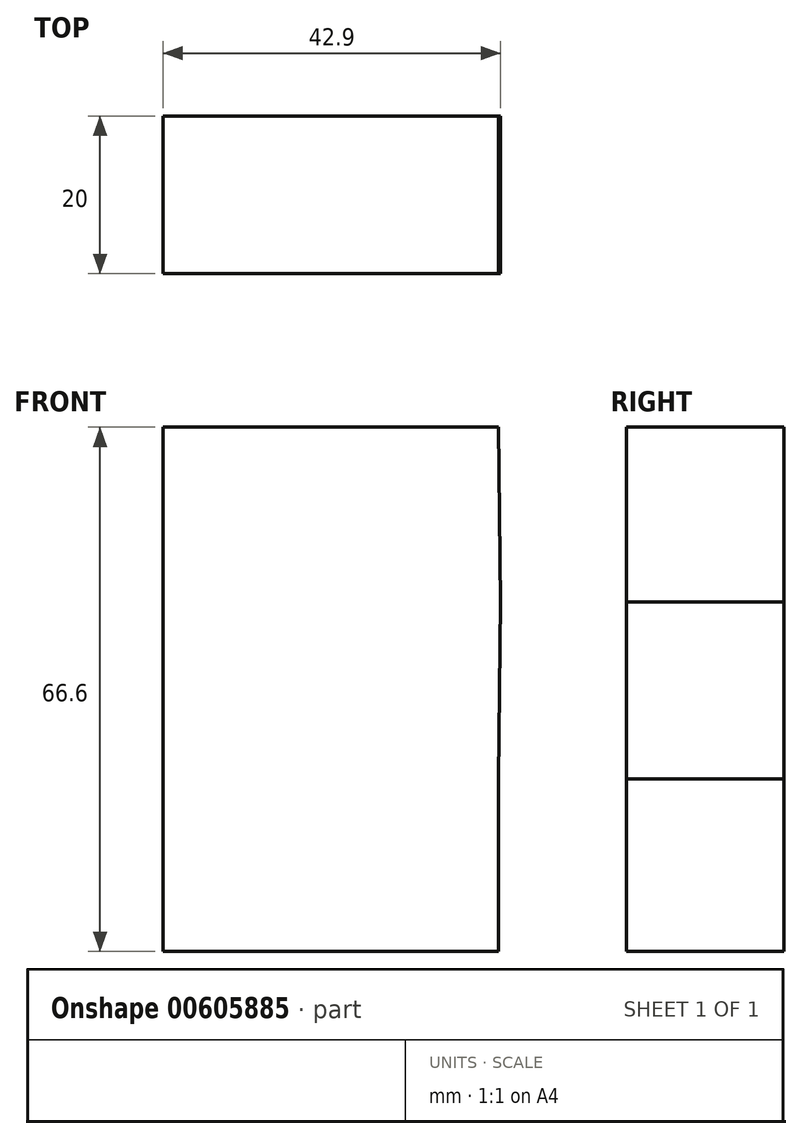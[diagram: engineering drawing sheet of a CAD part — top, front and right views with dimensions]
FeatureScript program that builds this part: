
annotation { "Feature Type Name" : "Feature", "Feature Type Description" : "" }
export const myFeature = defineFeature(function(context is Context, id is Id, definition is map)
    precondition{}
    {
        {
            var Q0;
            Q0=qCreatedBy(makeId("Front.planeOp"),FACE);
            var sketch = newSketch(context, id + "F0", { "sketchPlane" : qUnion([Q0])});
            skLineSegment(sketch, "E0", {"start": v(-5.55, 30.3) * mm, "end": v(-25.35, 30.3) * mm});
            skLineSegment(sketch, "E1", {"start": v(-25.35, 30.3) * mm, "end": v(-25.35, 8.1) * mm});
            skLineSegment(sketch, "E2", {"start": v(-25.35, 8.1) * mm, "end": v(-5.25, 8.1) * mm});
            skLineSegment(sketch, "E3", {"start": v(-5.55, 30.3) * mm, "end": v(-5.25, 8.1) * mm});
            skLineSegment(sketch, "E4", {"start": v(-25.35, 8.1) * mm, "end": v(-25.35, -14.4) * mm});
            skLineSegment(sketch, "E5", {"start": v(-25.35, -14.4) * mm, "end": v(-5.55, -14.4) * mm});
            skLineSegment(sketch, "E6", {"start": v(-5.55, -14.4) * mm, "end": v(-5.25, 8.1) * mm});
            skLineSegment(sketch, "E7", {"start": v(-25.35, -14.4) * mm, "end": v(-25.35, -36.3) * mm});
            skLineSegment(sketch, "E8", {"start": v(-25.35, -36.3) * mm, "end": v(-5.55, -36.3) * mm});
            skLineSegment(sketch, "E9", {"start": v(-5.55, -36.3) * mm, "end": v(-5.55, -14.4) * mm});
            skLineSegment(sketch, "E10", {"start": v(-25.35, 30.3) * mm, "end": v(-48.15, 30.3) * mm});
            skLineSegment(sketch, "E11", {"start": v(-48.15, 30.3) * mm, "end": v(-48.15, 8.1) * mm});
            skLineSegment(sketch, "E12", {"start": v(-25.35, 8.1) * mm, "end": v(-48.15, 8.1) * mm});
            skLineSegment(sketch, "E13", {"start": v(-48.15, 8.1) * mm, "end": v(-48.15, -14.4) * mm});
            skLineSegment(sketch, "E14", {"start": v(-48.15, -14.4) * mm, "end": v(-25.35, -14.4) * mm});
            skLineSegment(sketch, "E15", {"start": v(-48.15, -14.4) * mm, "end": v(-48.15, -36.3) * mm});
            skLineSegment(sketch, "E16", {"start": v(-48.15, -36.3) * mm, "end": v(-25.35, -36.3) * mm});
            skSolve(sketch);
        }
        {
            var Q0;
            Q0 = qSketchRegion(id + "F0", true);
            extrude(context, id + "F1", {"entities" : qUnion([Q0]), "depth" : 20 * mm, "offsetDistance" : 25 * mm});
        }
    });
